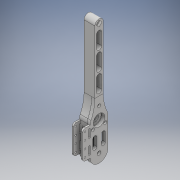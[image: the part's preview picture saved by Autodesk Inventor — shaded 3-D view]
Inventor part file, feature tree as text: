
AUTODESK INVENTOR PART (.ipt)
format: ipt  version: 2017 (Build 210142000, 142)  size: 413,184 bytes
history: native  units: mm
features: sketch x12, extrude x11, hole x5, other x2, mirror x2, fillet x2
ambient origin geometry x8: Origin, YZ Plane, XZ Plane, XY Plane, X Axis, Y Axis, Z Axis, Center Point
bodies: Body1 (feature_tree), Body2 (feature_tree)
feature tree (34):
  other  "Main"
  extrude  "Extrusion1"  Depth=54.4mm
  hole  "Hole1"  [1 undecoded]
  extrude  "Extrusion2"  Depth=16.0mm
  hole  "Hole3"  [1 undecoded]
  sketch  "Sketch3"  dims[d5=34.0mm d6=16.0mm]
  extrude  "Extrusion3"  Depth=6.6mm TaperAngle=0.0deg
  extrude  "Extrusion4"  Depth=6.0mm TaperAngle=0.0deg
  hole  "Hole4"  [1 undecoded]
  extrude  "Extrusion5"  Depth=12.0mm
  hole  "Hole5"  [1 undecoded]
  extrude  "Extrusion6"  Depth=10.0mm
  extrude  "Extrusion7"  Depth=10.0mm
  extrude  "Extrusion8"  Depth=5.0mm TaperAngle=0.0deg
  mirror  "Mirror1"
  extrude  "Extrusion9"  Depth=4.0mm TaperAngle=0.0deg
  extrude  "Extrusion10"  Depth=8.0mm
  hole  "Hole6"  [1 undecoded]
  mirror  "Mirror2"
  fillet  "Fillet2"  Radius=8.0mm
  fillet  "Fillet3"  Radius=16.0mm
  extrude  "Extrusion11"  Depth=8.0mm
  sketch  "Sketch1"  dims[d0=160.0mm d1=54.4mm]
  sketch  "Sketch2"  dims[d2=22.0mm d3=6.0mm]
  other  "Manifold"
  sketch  "Sketch4"  dims[d7=40.0mm d8=20.6mm d9=0.0mm]
  sketch  "Sketch5"  dims[d10=10.0mm d11=10.0mm]
  sketch  "Sketch6"  dims[d12=4.3mm d13=6.0mm d14=4.0mm d15=2.0mm d16=90.0deg d17=8.0mm d18=20.594885mm d28=6.6mm d29=0.0mm]
  sketch  "Sketch7"  dims[d30=10.0mm d31=10.0mm]
  sketch  "Sketch8"  dims[d32=12.0mm d33=6.0mm d34=4.0mm d35=2.0mm d36=90.0deg d37=8.0mm d38=20.594885mm d39=6.0mm d40=0.0mm]
  sketch  "Sketch9"  dims[d41=6.0mm d42=0.0mm]
  sketch  "Sketch10"  dims[d70=10.0mm d71=10.0mm d45=4.3mm d46=6.0mm d47=7.1mm d48=4.1mm d49=90.0deg d50=8.0mm d51=20.594885mm d53=10.0mm]
  sketch  "Sketch11"  dims[d54=8.6mm d55=0.0mm d56=12.0mm]
  sketch  "Sketch12"  dims[d57=12.0mm d58=24.0mm d59=10.0mm d60=10.0mm d61=3.2mm d62=6.0mm d63=6.0mm d64=3.2mm d65=90.0deg d66=8.0mm d67=20.594885mm d68=5.0mm d69=0.0mm d72=4.0mm d73=0.0mm d74=8.0mm d75=4.0mm d76=0.0mm d77=8.0mm d78=16.0mm d79=8.0mm d80=10.0mm d81=0.0mm d82=14.0mm d83=3.0mm d84=1.5mm d85=6.0mm d86=6.0mm d88=42.4mm d89=14.133333mm d90=14.133333mm d91=3.0mm d92=0.0mm d93=4.0mm d94=6.0mm d95=6.0mm d96=42.4mm d97=14.133333mm d98=14.133333mm d99=3.2mm d100=6.0mm d101=4.0mm d102=2.0mm d103=90.0deg d104=8.0mm d105=20.594885mm d107=5.0mm d108=11.0mm d109=3.0mm d110=13.0mm d111=13.0mm d112=23.0mm d113=23.0mm d114=23.0mm d115=16.0mm d116=3.0mm d117=0.0mm]
note: 5 required parameter values undecoded (feature->parameter linkage not recoverable at this tier; creation-order binding heuristic only, values carry confidence <= 0.55)
